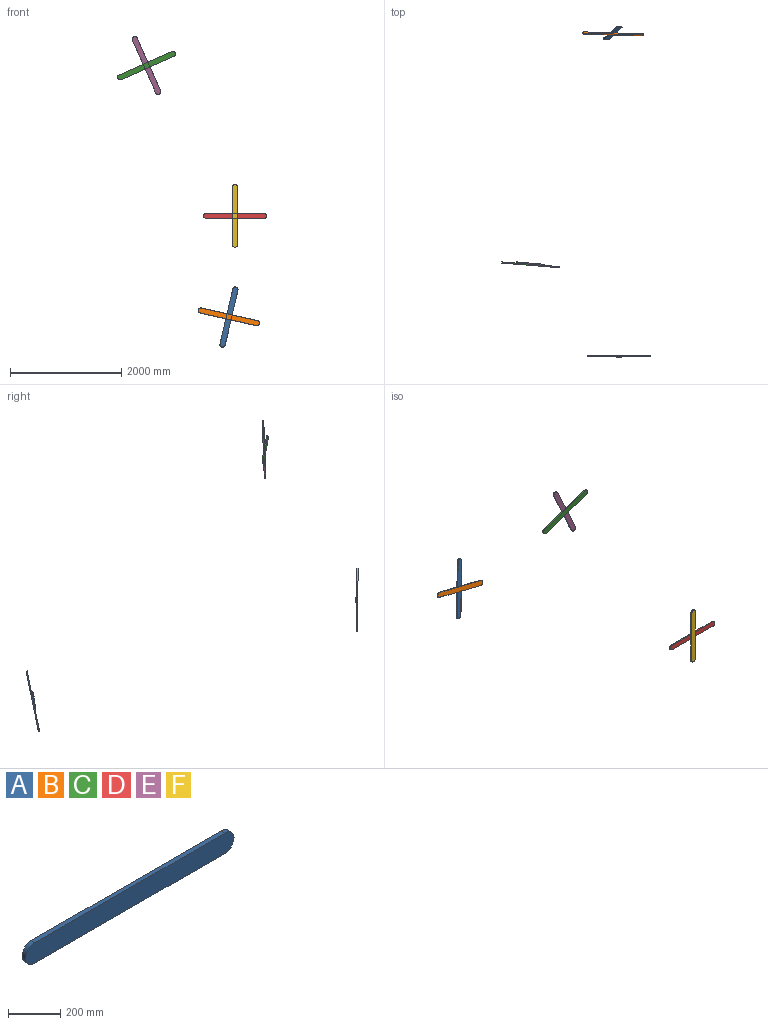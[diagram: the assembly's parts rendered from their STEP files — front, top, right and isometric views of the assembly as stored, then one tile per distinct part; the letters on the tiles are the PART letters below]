
ASSEMBLY  parts=6 mates=3
PART A: 6 faces, bbox 1127.1x20.3x95.3 mm
  f0: cylinder r=47.62mm len=95.25mm, axis (0,1,0), area 3040.2mm2, adj f1,f3,f4,f5
  f1: plane 1031.88x20.32mm, normal (0,0,1), area 20967.7mm2, adj f0,f2,f4,f5
  f2: cylinder r=47.62mm len=95.25mm, axis (0,1,0), area 3040.2mm2, adj f1,f3,f4,f5
  f3: plane 1031.88x20.32mm, normal (0,0,-1), area 20967.7mm2, adj f0,f2,f4,f5
  f4: plane 1127.13x95.25mm, normal (0,-1,0), area 105411.7mm2, adj f0,f1,f2,f3
  f5: plane 1127.13x95.25mm, normal (0,1,0), area 105411.7mm2, adj f0,f1,f2,f3
PART B: same geometry as A
PART C: same geometry as A
PART D: same geometry as A
PART E: same geometry as A
PART F: same geometry as A
PLACE A rot(axis=(0.62,-0.07,-0.78),172.3deg) t=(-8439.6,4924.51,-8377.91)mm
PLACE B rot(axis=(-0.67,0.74,-0.03),17.2deg) t=(338.25,6135.22,-2978.42)mm
PLACE C rot(axis=(0.98,-0.04,0.21),179deg) t=(-982.03,1177.95,-260.36)mm
PLACE D at identity
PLACE E rot(axis=(-0.84,0.03,0.54),177.5deg) t=(-6766.02,1667.18,-5269.88)mm
PLACE F rot(axis=(0,1,0),90deg) t=(-2225.59,-20.32,-7337.27)mm
MATE fastened A.f5 <-> B.f5  axis (0.01,-0.98,0.2) through (-4889.67,5784.52,-4371.32)mm
MATE fastened F.f5 <-> D.f4  axis (0,1,0) through (-4781.43,-20.32,-2555.84)mm
MATE planar E.f5 <-> C.f4  axis (-0.08,-1,0) through (-6369.78,1635.06,137.19)mm
